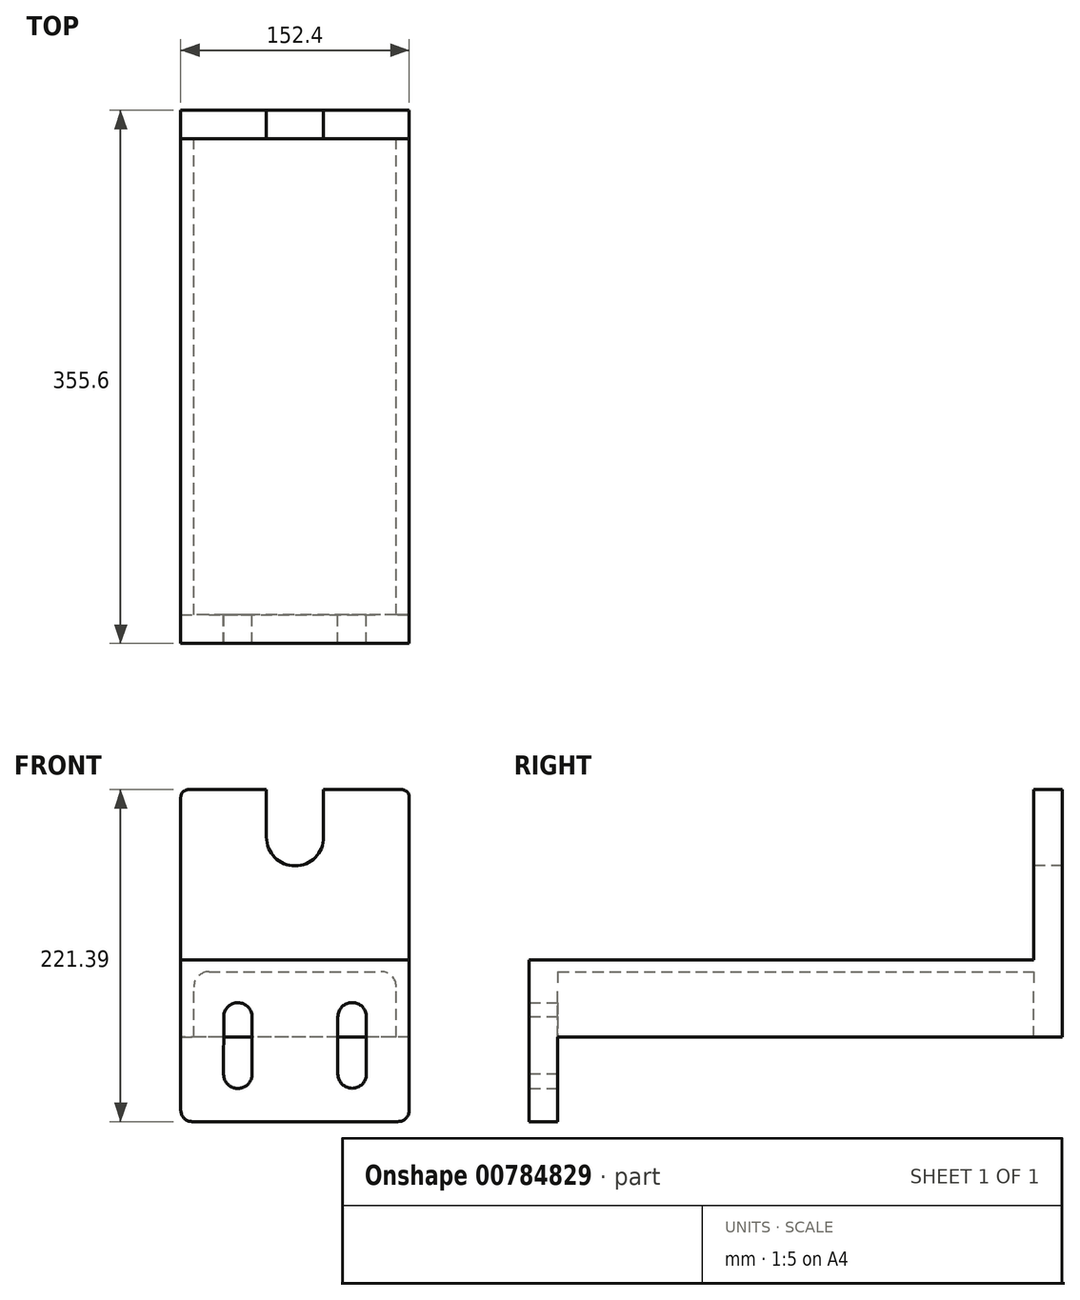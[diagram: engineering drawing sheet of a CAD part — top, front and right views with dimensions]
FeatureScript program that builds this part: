
annotation { "Feature Type Name" : "Feature", "Feature Type Description" : "" }
export const myFeature = defineFeature(function(context is Context, id is Id, definition is map)
    precondition{}
    {
        {
            var Q0;
            Q0=qCreatedBy(makeId("Front.planeOp"),FACE);
            var sketch = newSketch(context, id + "F0", { "sketchPlane" : qUnion([Q0])});
            skLineSegment(sketch, "E0", {"start": v(0, 0) * mm, "end": v(152.4, 0) * mm});
            skLineSegment(sketch, "E1", {"start": v(0, 0) * mm, "end": v(0, -51.66) * mm});
            skLineSegment(sketch, "E2", {"start": v(0, -51.66) * mm, "end": v(8.71, -51.66) * mm});
            skLineSegment(sketch, "E3", {"start": v(8.71, -51.66) * mm, "end": v(8.71, -18.14) * mm});
            skLineSegment(sketch, "E4", {"start": v(18.87, -7.98) * mm, "end": v(133.53, -7.98) * mm});
            skLineSegment(sketch, "E5", {"start": v(152.4, 0) * mm, "end": v(152.4, -51.66) * mm});
            skLineSegment(sketch, "E6", {"start": v(152.4, -51.66) * mm, "end": v(143.69, -51.66) * mm});
            skLineSegment(sketch, "E7", {"start": v(143.69, -51.66) * mm, "end": v(143.69, -18.14) * mm});
            skPoint(sketch, "E8.visualSharp", {"position": v(8.71, -7.98) * mm});
            skArc(sketch, "E8.filletArc", {"start": v(18.87, -7.98) * mm, "mid": v(11.69, -10.95) * mm, "end": v(8.71, -18.14) * mm});
            skPoint(sketch, "E9.visualSharp", {"position": v(143.69, -7.98) * mm});
            skArc(sketch, "E9.filletArc", {"start": v(143.69, -18.14) * mm, "mid": v(140.71, -10.95) * mm, "end": v(133.53, -7.98) * mm});
            skSolve(sketch);
        }
        {
            var Q0;
            Q0=makeQuery(id+"F0.imprint","IMPRINT",FACE,{"disambiguationData":[TD([[makeQuery(id+"F0.imprint","IMPRINT",EDGE,{"derivedFrom":sQuery(id+"F0.wireOp",EDGE,"E0")}),-1.0]])]});
            extrude(context, id + "F1", {"entities" : qUnion([Q0]), "depth" : 317.5 * mm, "offsetDistance" : 25.4 * mm});
        }
        {
            var Q0;
            Q0=makeQuery(id+"F1.opExtrude","CAP_FACE",FACE,{"disambiguationData":[OSD([sQuery(id+"F0.wireOp",EDGE,"E0"),sQuery(id+"F0.wireOp",EDGE,"E1"),sQuery(id+"F0.wireOp",EDGE,"E2"),sQuery(id+"F0.wireOp",EDGE,"E3"),sQuery(id+"F0.wireOp",EDGE,"E4"),sQuery(id+"F0.wireOp",EDGE,"E5"),sQuery(id+"F0.wireOp",EDGE,"E6"),sQuery(id+"F0.wireOp",EDGE,"E7"),sQuery(id+"F0.wireOp",EDGE,"E8.filletArc"),sQuery(id+"F0.wireOp",EDGE,"E9.filletArc")])],"isStart":false});
            var sketch = newSketch(context, id + "F2", { "sketchPlane" : qUnion([Q0])});
            skLineSegment(sketch, "E10.0", {"start": v(0, 0) * mm, "end": v(152.4, 0) * mm});
            skLineSegment(sketch, "E11", {"start": v(152.4, 0) * mm, "end": v(152.4, -100.33) * mm});
            skLineSegment(sketch, "E12", {"start": v(0, 0) * mm, "end": v(0, -100.33) * mm});
            skLineSegment(sketch, "E13", {"start": v(144.78, -107.95) * mm, "end": v(7.62, -107.95) * mm});
            skPoint(sketch, "E14.visualSharp", {"position": v(152.4, -107.95) * mm});
            skArc(sketch, "E14.filletArc", {"start": v(144.78, -107.95) * mm, "mid": v(150.17, -105.72) * mm, "end": v(152.4, -100.33) * mm});
            skPoint(sketch, "E15.visualSharp", {"position": v(0, -107.95) * mm});
            skArc(sketch, "E15.filletArc", {"start": v(0, -100.33) * mm, "mid": v(2.23, -105.72) * mm, "end": v(7.62, -107.95) * mm});
            skLineSegment(sketch, "E16", {"start": v(114.3, -107.95) * mm, "end": v(114.3, 0) * mm, "construction": true});
            skLineSegment(sketch, "E17", {"start": v(38.1, -107.95) * mm, "end": v(38.1, 0) * mm, "construction": true});
            skLineSegment(sketch, "E18.left", {"start": v(104.77, -38.1) * mm, "end": v(104.78, -76.2) * mm});
            skLineSegment(sketch, "E18.right", {"start": v(123.82, -38.1) * mm, "end": v(123.83, -76.2) * mm});
            skPoint(sketch, "E18.middle", {"position": v(114.3, -57.15) * mm});
            skLineSegment(sketch, "E19.left", {"start": v(28.6, -37.99) * mm, "end": v(28.56, -76.09) * mm});
            skLineSegment(sketch, "E19.right", {"start": v(47.64, -38.21) * mm, "end": v(47.6, -76.31) * mm});
            skPoint(sketch, "E19.middle", {"position": v(38.1, -57.15) * mm});
            skLineSegment(sketch, "E20", {"start": v(114.3, -57.15) * mm, "end": v(38.1, -57.15) * mm, "construction": true});
            skArc(sketch, "E21", {"start": v(123.82, -38.1) * mm, "mid": v(114.3, -28.58) * mm, "end": v(104.77, -38.1) * mm});
            skArc(sketch, "E22", {"start": v(123.83, -76.2) * mm, "mid": v(114.3, -85.73) * mm, "end": v(104.78, -76.2) * mm});
            skArc(sketch, "E23", {"start": v(47.6, -76.31) * mm, "mid": v(37.97, -85.83) * mm, "end": v(28.56, -76.09) * mm});
            skArc(sketch, "E24", {"start": v(47.64, -38.21) * mm, "mid": v(38.23, -28.68) * mm, "end": v(28.6, -37.99) * mm});
            skLineSegment(sketch, "E25", {"start": v(76.2, -107.95) * mm, "end": v(76.2, 0) * mm, "construction": true});
            skCircle(sketch, "E26", {"center": v(76.2, -57.15) * mm, "radius": 2.01 * mm, "construction": true});
            skSolve(sketch);
        }
        {
            var Q0;
            Q0=makeQuery(id+"F1.opExtrude","CAP_FACE",FACE,{"disambiguationData":[OSD([sQuery(id+"F0.wireOp",EDGE,"E0"),sQuery(id+"F0.wireOp",EDGE,"E1"),sQuery(id+"F0.wireOp",EDGE,"E2"),sQuery(id+"F0.wireOp",EDGE,"E3"),sQuery(id+"F0.wireOp",EDGE,"E4"),sQuery(id+"F0.wireOp",EDGE,"E5"),sQuery(id+"F0.wireOp",EDGE,"E6"),sQuery(id+"F0.wireOp",EDGE,"E7"),sQuery(id+"F0.wireOp",EDGE,"E8.filletArc"),sQuery(id+"F0.wireOp",EDGE,"E9.filletArc")])],"isStart":true});
            var sketch = newSketch(context, id + "F3", { "sketchPlane" : qUnion([Q0])});
            skLineSegment(sketch, "E27", {"start": v(-152.4, -51.66) * mm, "end": v(0, -51.66) * mm});
            skLineSegment(sketch, "E28", {"start": v(-152.4, -51.66) * mm, "end": v(-152.4, 108.36) * mm});
            skLineSegment(sketch, "E29", {"start": v(0, -51.66) * mm, "end": v(0, 108.36) * mm});
            skPoint(sketch, "E29.endSnap0", {"position": v(0, -25.83) * mm});
            skLineSegment(sketch, "E30", {"start": v(-147.32, 113.44) * mm, "end": v(-95.25, 113.44) * mm});
            skLineSegment(sketch, "E31", {"start": v(-95.25, 113.44) * mm, "end": v(-95.25, 81.69) * mm});
            skLineSegment(sketch, "E32", {"start": v(-5.08, 113.44) * mm, "end": v(-57.15, 113.44) * mm});
            skLineSegment(sketch, "E33", {"start": v(-57.15, 113.44) * mm, "end": v(-57.15, 81.69) * mm});
            skArc(sketch, "E34", {"start": v(-95.25, 81.69) * mm, "mid": v(-76.2, 62.64) * mm, "end": v(-57.15, 81.69) * mm});
            skPoint(sketch, "E35.visualSharp", {"position": v(-152.4, 113.44) * mm});
            skArc(sketch, "E35.filletArc", {"start": v(-147.32, 113.44) * mm, "mid": v(-150.91, 111.95) * mm, "end": v(-152.4, 108.36) * mm});
            skPoint(sketch, "E36.visualSharp", {"position": v(0, 113.44) * mm});
            skArc(sketch, "E36.filletArc", {"start": v(0, 108.36) * mm, "mid": v(-1.49, 111.95) * mm, "end": v(-5.08, 113.44) * mm});
            skSolve(sketch);
        }
        {
            var Q0;
            Q0=makeQuery(id+"F3.imprint","IMPRINT",FACE,{"disambiguationData":[TD([[makeQuery(id+"F3.imprint","IMPRINT",EDGE,{"derivedFrom":sQuery(id+"F3.wireOp",EDGE,"E30")}),-1.0]])]});
            var Q1;
            {var subQ1=makeQuery(id+"F1.opExtrude","CAP_EDGE",EDGE,{"disambiguationData":[OSD([sQuery(id+"F0.wireOp",EDGE,"E3")])],"isStart":true});Q1=makeQuery(id+"F3.imprint","IMPRINT",FACE,{"disambiguationData":[TD([[makeQuery(id+"F3.imprint","IMPRINT",EDGE,{"derivedFrom":subQ1}),1.0]])]});}
            var Q2;
            Q2=makeQuery(id+"FprGDL18OlgBvfN_1.opExtrude","CAP_FACE",FACE,{"disambiguationData":[OSD([sQuery(id+"F2.wireOp",EDGE,"E10.0"),sQuery(id+"F2.wireOp",EDGE,"E11"),sQuery(id+"F2.wireOp",EDGE,"E12"),sQuery(id+"F2.wireOp",EDGE,"E13"),sQuery(id+"F2.wireOp",EDGE,"E14.filletArc"),sQuery(id+"F2.wireOp",EDGE,"E15.filletArc"),sQuery(id+"F2.wireOp",EDGE,"E18.left"),sQuery(id+"F2.wireOp",EDGE,"E18.right"),sQuery(id+"F2.wireOp",EDGE,"E19.left"),sQuery(id+"F2.wireOp",EDGE,"E19.right"),sQuery(id+"F2.wireOp",EDGE,"E21"),sQuery(id+"F2.wireOp",EDGE,"E22"),sQuery(id+"F2.wireOp",EDGE,"E23"),sQuery(id+"F2.wireOp",EDGE,"E24")])],"isStart":true});
            var Q3;
            {var subQ1=makeQuery(id+"F1.opExtrude","CAP_EDGE",EDGE,{"disambiguationData":[OSD([sQuery(id+"F0.wireOp",EDGE,"E0")])],"isStart":true});Q3=makeQuery(id+"F3.imprint","IMPRINT",FACE,{"disambiguationData":[TD([[makeQuery(id+"F3.imprint","IMPRINT",EDGE,{"derivedFrom":subQ1}),1.0]])]});}
            extrude(context, id + "F4", {"entities" : qUnion([Q0, Q1, Q2, Q3]), "operationType" : NewBodyOperationType.ADD, "depth" : 19.05 * mm, "offsetDistance" : 25.4 * mm});
        }
        {
            var Q0;
            Q0 = qSketchRegion(id + "F2", true);
            extrude(context, id + "F5", {"entities" : qUnion([Q0]), "operationType" : NewBodyOperationType.ADD, "depth" : 19.05 * mm, "offsetDistance" : 25.4 * mm});
        }
    });
